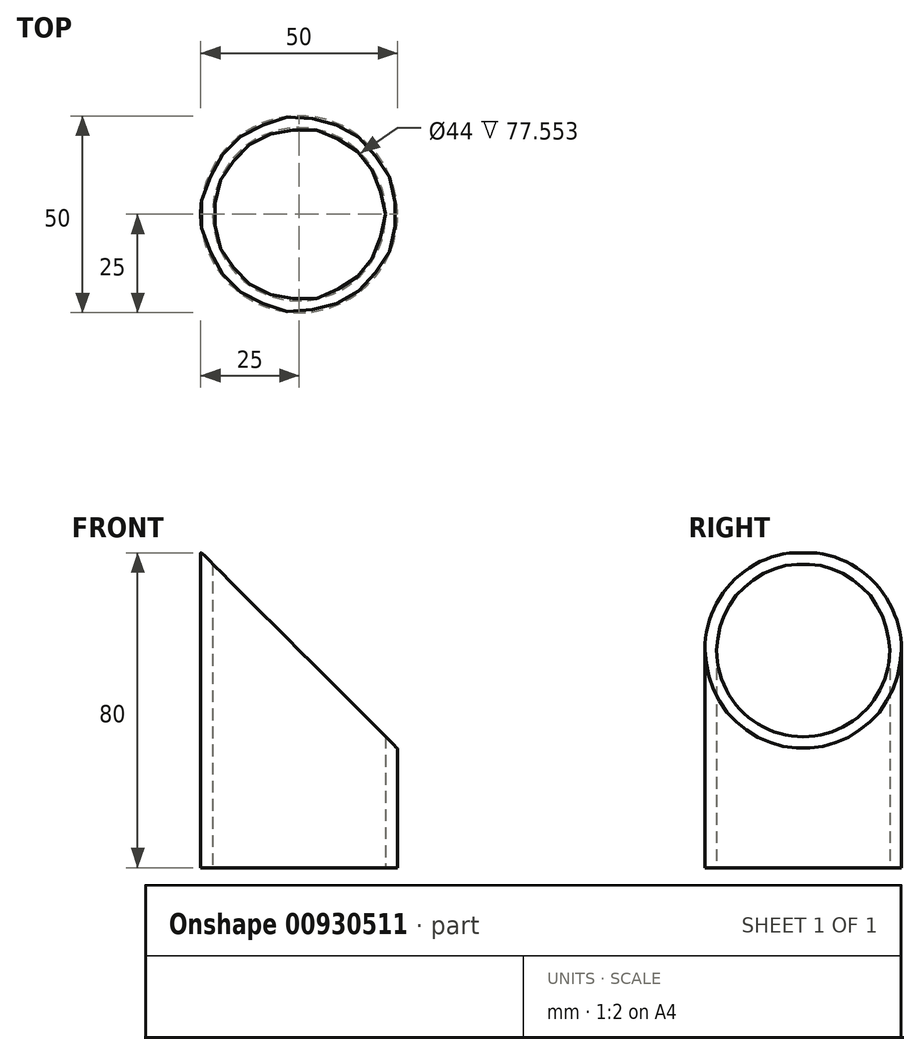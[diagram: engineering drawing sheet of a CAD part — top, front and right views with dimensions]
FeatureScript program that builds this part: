
annotation { "Feature Type Name" : "Feature", "Feature Type Description" : "" }
export const myFeature = defineFeature(function(context is Context, id is Id, definition is map)
    precondition{}
    {
        {
            var Q0;
            Q0=qCreatedBy(makeId("Top.planeOp"),FACE);
            var sketch = newSketch(context, id + "F0", { "sketchPlane" : qUnion([Q0])});
            skCircle(sketch, "E0", {"center": v(0, 0) * mm, "radius": 25 * mm});
            skCircle(sketch, "E1", {"center": v(0, 0) * mm, "radius": 22 * mm});
            skSolve(sketch);
        }
        {
            var Q0;
            Q0=qSketchRegion(id+"F0",true);
            extrude(context, id + "F1", {"entities" : qUnion([Q0]), "depth" : 80 * mm, "offsetDistance" : 25 * mm});
        }
        {
            var Q0;
            Q0=qCreatedBy(makeId("Front.planeOp"),FACE);
            var sketch = newSketch(context, id + "F2", { "sketchPlane" : qUnion([Q0])});
            skLineSegment(sketch, "E2", {"start": v(-24.92, 80.17) * mm, "end": v(25.08, 30.17) * mm});
            skLineSegment(sketch, "E3", {"start": v(25.08, 30.17) * mm, "end": v(25.08, 80.17) * mm});
            skLineSegment(sketch, "E4", {"start": v(25.08, 80.17) * mm, "end": v(-24.92, 80.17) * mm});
            skSolve(sketch);
        }
        {
            var Q0;
            Q0=qSketchRegion(id+"F2",true);
            extrude(context, id + "F3", {"entities" : qUnion([Q0]), "operationType" : NewBodyOperationType.REMOVE, "endBound" : BoundingType.SYMMETRIC, "oppositeDirection" : true, "depth" : 80 * mm, "offsetDistance" : 25 * mm});
        }
    });
